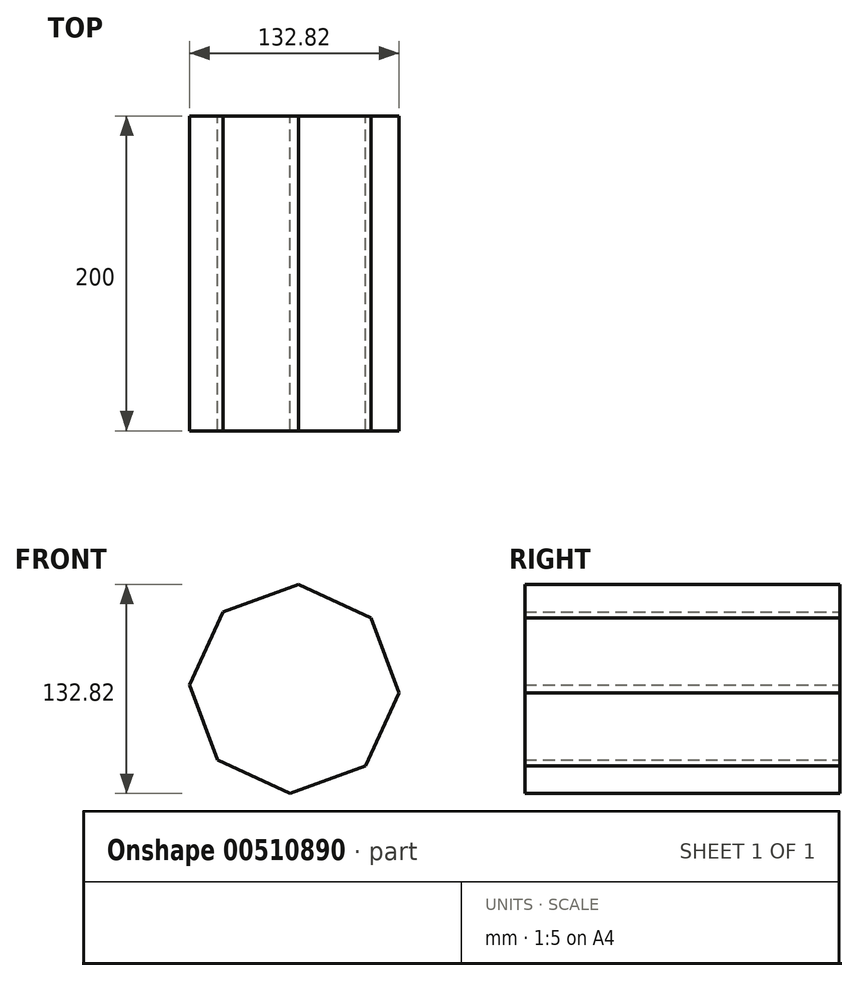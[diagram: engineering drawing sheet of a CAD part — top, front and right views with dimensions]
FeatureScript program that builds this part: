
annotation { "Feature Type Name" : "Feature", "Feature Type Description" : "" }
export const myFeature = defineFeature(function(context is Context, id is Id, definition is map)
    precondition{}
    {
        {
            var Q0;
            Q0=qCreatedBy(makeId("Front.planeOp"),FACE);
            var sketch = newSketch(context, id + "F0", { "sketchPlane" : qUnion([Q0])});
            skCircle(sketch, "E0.cCircle", {"center": v(0, 0) * mm, "radius": 66.46 * mm, "construction": true});
            skLineSegment(sketch, "E0.0", {"start": v(-2.58, -66.41) * mm, "end": v(-48.79, -45.14) * mm});
            skLineSegment(sketch, "E0.1", {"start": v(-48.79, -45.14) * mm, "end": v(-66.41, 2.58) * mm});
            skLineSegment(sketch, "E0.2", {"start": v(-66.41, 2.58) * mm, "end": v(-45.14, 48.79) * mm});
            skLineSegment(sketch, "E0.3", {"start": v(-45.14, 48.79) * mm, "end": v(2.58, 66.41) * mm});
            skLineSegment(sketch, "E0.4", {"start": v(2.58, 66.41) * mm, "end": v(48.79, 45.14) * mm});
            skLineSegment(sketch, "E0.5", {"start": v(48.79, 45.14) * mm, "end": v(66.41, -2.58) * mm});
            skLineSegment(sketch, "E0.6", {"start": v(66.41, -2.58) * mm, "end": v(45.14, -48.79) * mm});
            skLineSegment(sketch, "E0.7", {"start": v(45.14, -48.79) * mm, "end": v(-2.58, -66.41) * mm});
            skSolve(sketch);
        }
        {
            var Q0;
            Q0=qSketchRegion(id+"F0",true);
            extrude(context, id + "F1", {"entities" : qUnion([Q0]), "depth" : 200 * mm});
        }
    });
